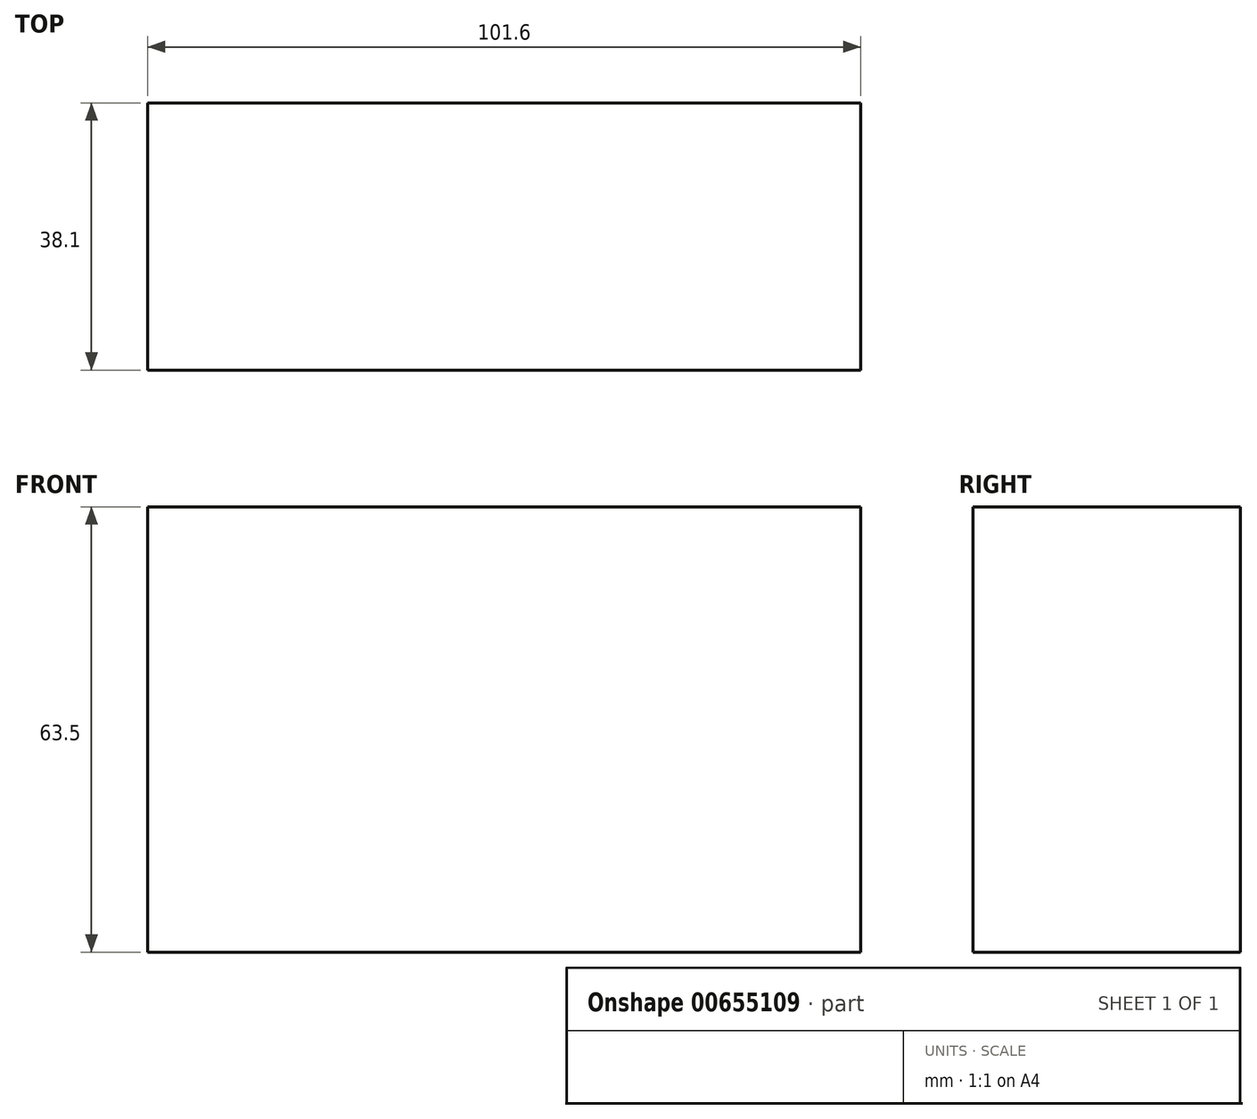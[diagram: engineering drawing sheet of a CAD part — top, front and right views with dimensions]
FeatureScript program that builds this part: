
annotation { "Feature Type Name" : "Feature", "Feature Type Description" : "" }
export const myFeature = defineFeature(function(context is Context, id is Id, definition is map)
    precondition{}
    {
        {
            var Q0;
            Q0=qCreatedBy(makeId("Front.planeOp"),FACE);
            var sketch = newSketch(context, id + "F0", { "sketchPlane" : qUnion([Q0])});
            skLineSegment(sketch, "E0.bottom", {"start": v(-50.8, 31.75) * mm, "end": v(50.8, 31.75) * mm});
            skLineSegment(sketch, "E0.top", {"start": v(-50.8, -31.75) * mm, "end": v(50.8, -31.75) * mm});
            skLineSegment(sketch, "E0.left", {"start": v(-50.8, 31.75) * mm, "end": v(-50.8, -31.75) * mm});
            skLineSegment(sketch, "E0.right", {"start": v(50.8, 31.75) * mm, "end": v(50.8, -31.75) * mm});
            skPoint(sketch, "E0.middle", {"position": v(0, 0) * mm});
            skSolve(sketch);
        }
        {
            var Q0;
            Q0 = qSketchRegion(id + "F0", true);
            extrude(context, id + "F1", {"entities" : qUnion([Q0]), "depth" : 38.1 * mm, "offsetDistance" : 25.4 * mm});
        }
    });
